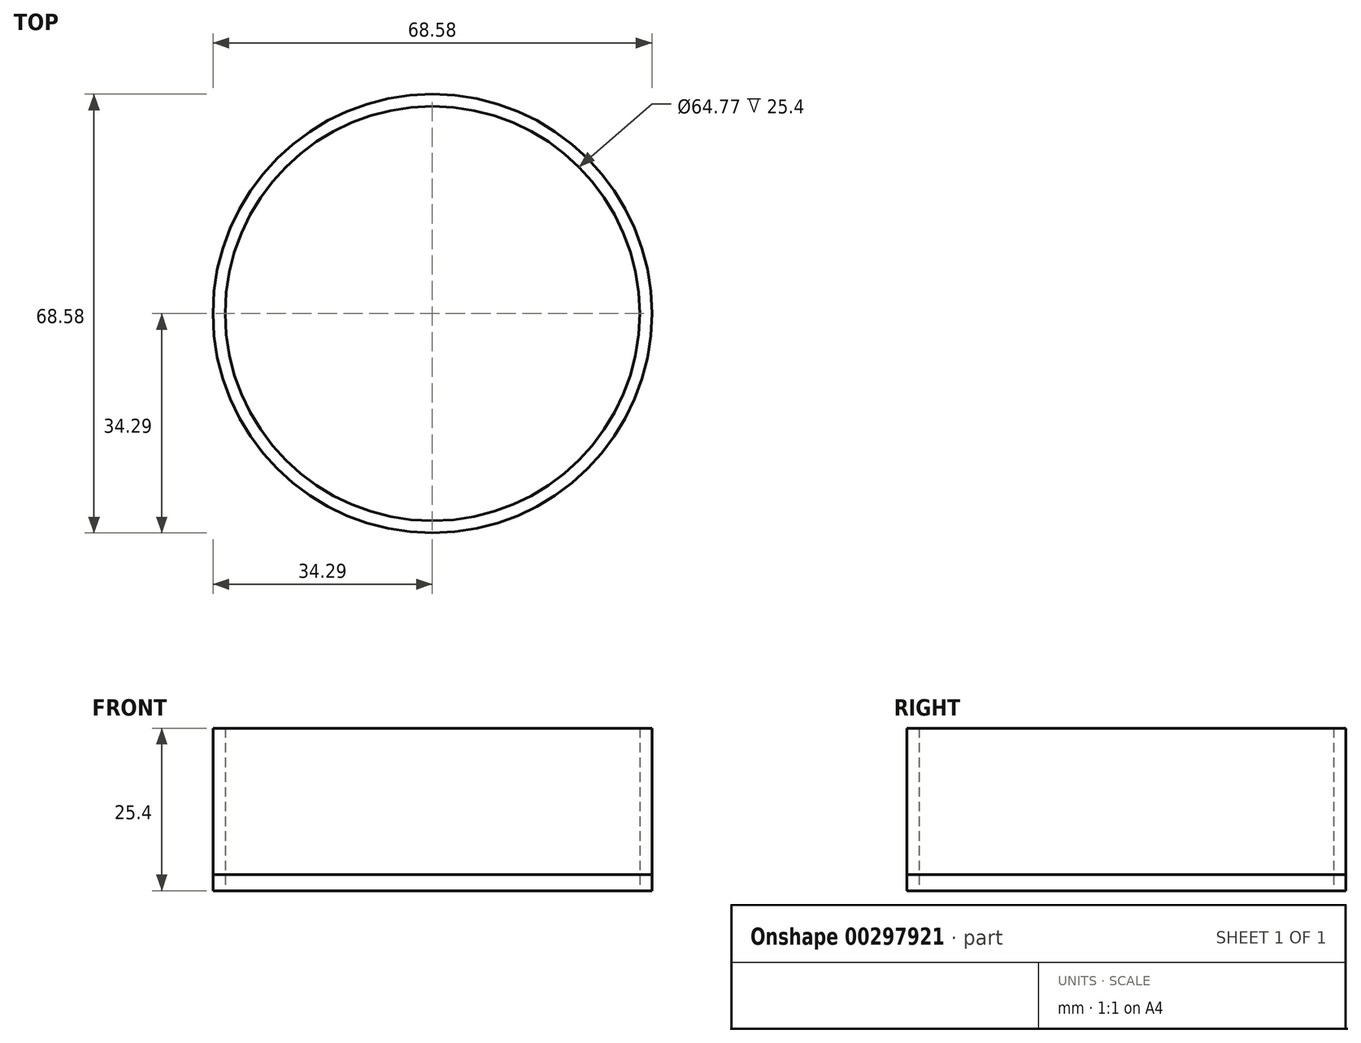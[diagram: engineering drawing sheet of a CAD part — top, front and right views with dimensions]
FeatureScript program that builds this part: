
annotation { "Feature Type Name" : "Feature", "Feature Type Description" : "" }
export const myFeature = defineFeature(function(context is Context, id is Id, definition is map)
    precondition{}
    {
        {
            var Q0;
            Q0=qCreatedBy(makeId("Top.planeOp"),FACE);
            var sketch = newSketch(context, id + "F0", { "sketchPlane" : qUnion([Q0])});
            skCircle(sketch, "E0", {"center": v(0, 0) * mm, "radius": 34.3 * mm});
            skCircle(sketch, "E1", {"center": v(0, 0) * mm, "radius": 32.39 * mm});
            skSolve(sketch);
        }
        {
            var Q0;
            Q0 = qSketchRegion(id + "F0", true);
            var Q1;
            Q1=makeQuery(id+"F0.imprint","IMPRINT",FACE,{"disambiguationData":[TD([[makeQuery(id+"F0.imprint","IMPRINT",EDGE,{"derivedFrom":sQuery(id+"F0.wireOp",EDGE,"E1")}),1.0]])]});
            extrude(context, id + "F1", {"entities" : qUnion([Q0, Q1]), "depth" : 2.54 * mm});
        }
        {
            var Q0;
            Q0 = qSketchRegion(id + "F0", true);
            extrude(context, id + "F2", {"entities" : qUnion([Q0]), "depth" : 25.4 * mm});
        }
    });
